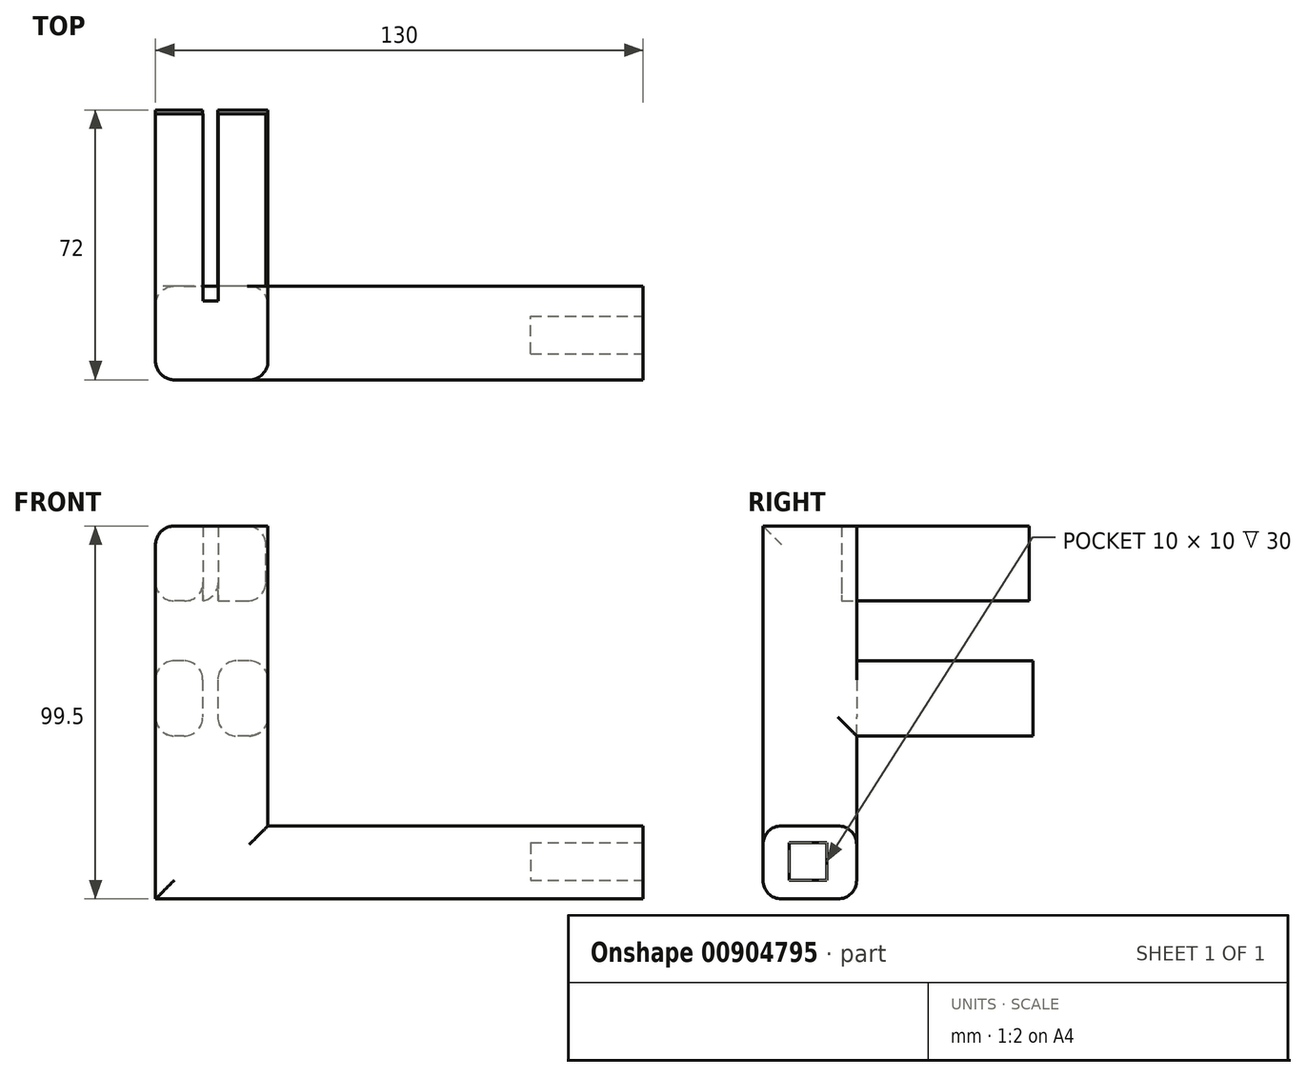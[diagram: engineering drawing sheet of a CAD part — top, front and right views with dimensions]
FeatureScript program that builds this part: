
annotation { "Feature Type Name" : "Feature", "Feature Type Description" : "" }
export const myFeature = defineFeature(function(context is Context, id is Id, definition is map)
    precondition{}
    {
        {
            var Q0;
            Q0=qCreatedBy(makeId("Front.planeOp"),FACE);
            var sketch = newSketch(context, id + "F0", { "sketchPlane" : qUnion([Q0])});
            skLineSegment(sketch, "E0", {"start": v(40.24, -41.34) * mm, "end": v(40.24, -41.2) * mm});
            skLineSegment(sketch, "E1", {"start": v(40.24, -41.34) * mm, "end": v(-89.76, -41.34) * mm});
            skLineSegment(sketch, "E2", {"start": v(-89.76, 58.16) * mm, "end": v(-59.76, 58.16) * mm});
            skLineSegment(sketch, "E3", {"start": v(-59.76, -21.84) * mm, "end": v(40.24, -21.84) * mm});
            skLineSegment(sketch, "E4", {"start": v(40.24, -21.84) * mm, "end": v(40.24, -41.2) * mm});
            skLineSegment(sketch, "E5", {"start": v(-59.76, 58.16) * mm, "end": v(-59.76, -21.84) * mm});
            skLineSegment(sketch, "E6", {"start": v(-89.76, 58.16) * mm, "end": v(-89.76, -41.34) * mm});
            skSolve(sketch);
        }
        {
            var Q0;
            Q0=makeQuery(id+"F0.imprint","IMPRINT",FACE,{"disambiguationData":[TD([[makeQuery(id+"F0.imprint","IMPRINT",EDGE,{"derivedFrom":sQuery(id+"F0.wireOp",EDGE,"E0")}),1.0]])]});
            extrude(context, id + "F1", {"entities" : qUnion([Q0]), "depth" : 25 * mm, "offsetDistance" : 25 * mm});
        }
        {
            var Q0;
            Q0=makeQuery(id+"F1.opExtrude","SWEPT_FACE",FACE,{"disambiguationData":[OSD([sQuery(id+"F0.wireOp",EDGE,"E2")])]});
            var sketch = newSketch(context, id + "F2", { "sketchPlane" : qUnion([Q0])});
            skLineSegment(sketch, "E7.bottom", {"start": v(-89.76, 46) * mm, "end": v(-60.31, 46) * mm});
            skLineSegment(sketch, "E7.top", {"start": v(-89.76, -9) * mm, "end": v(-60.31, -9) * mm});
            skLineSegment(sketch, "E7.left", {"start": v(-89.76, 46) * mm, "end": v(-89.76, -9) * mm});
            skLineSegment(sketch, "E7.right", {"start": v(-60.31, 46) * mm, "end": v(-60.31, -9) * mm});
            skSolve(sketch);
        }
        {
            var Q0;
            {var subQ0=sQuery(id+"F2.wireOp",EDGE,"E7.top");Q0=makeQuery(id+"F2.imprint","IMPRINT",FACE,{"disambiguationData":[TD([[makeQuery(id+"F2.imprint","IMPRINT",EDGE,{"derivedFrom":subQ0}),1.0]])]});}
            var Q1;
            {var subQ0=sQuery(id+"F2.wireOp",EDGE,"E7.bottom");Q1=makeQuery(id+"F2.imprint","IMPRINT",FACE,{"disambiguationData":[TD([[makeQuery(id+"F2.imprint","IMPRINT",EDGE,{"derivedFrom":subQ0}),-1.0]])]});}
            extrude(context, id + "F3", {"entities" : qUnion([Q0, Q1]), "operationType" : NewBodyOperationType.ADD, "oppositeDirection" : true, "depth" : 20 * mm, "offsetDistance" : 25 * mm});
        }
        {
            var Q0;
            Q0=makeQuery(id+"F3.opExtrude","SWEPT_FACE",FACE,{"disambiguationData":[OSD([sQuery(id+"F2.wireOp",EDGE,"E7.bottom")])]});
            var sketch = newSketch(context, id + "F4", { "sketchPlane" : qUnion([Q0])});
            skLineSegment(sketch, "E8.bottom", {"start": v(73.04, 58.16) * mm, "end": v(77.04, 58.16) * mm});
            skLineSegment(sketch, "E8.top", {"start": v(73.04, 38.16) * mm, "end": v(77.04, 38.16) * mm});
            skLineSegment(sketch, "E9", {"start": v(77.04, 58.16) * mm, "end": v(77.04, 38.16) * mm});
            skLineSegment(sketch, "E10", {"start": v(73.04, 58.16) * mm, "end": v(73.04, 38.16) * mm});
            skSolve(sketch);
        }
        {
            var Q0;
            Q0=makeQuery(id+"F4.imprint","IMPRINT",FACE,{"disambiguationData":[TD([[makeQuery(id+"F4.imprint","IMPRINT",EDGE,{"derivedFrom":sQuery(id+"F4.wireOp",EDGE,"E8.top")}),-1.0]])]});
            extrude(context, id + "F5", {"entities" : qUnion([Q0]), "operationType" : NewBodyOperationType.REMOVE, "oppositeDirection" : true, "depth" : 50 * mm, "offsetDistance" : 25 * mm});
        }
        {
            var Q0;
            Q0=makeQuery(id+"F1.opExtrude","CAP_FACE",FACE,{"disambiguationData":[OSD([sQuery(id+"F0.wireOp",EDGE,"E0"),sQuery(id+"F0.wireOp",EDGE,"E1"),sQuery(id+"F0.wireOp",EDGE,"0686c2bd-6ec9-4ceb-ab54-b0329b36704b"),sQuery(id+"F0.wireOp",EDGE,"E2"),sQuery(id+"F0.wireOp",EDGE,"96b1564c-ce13-4406-9d07-ae3dbd072935"),sQuery(id+"F0.wireOp",EDGE,"E3"),sQuery(id+"F0.wireOp",EDGE,"E4")])],"isStart":true});
            var sketch = newSketch(context, id + "F6", { "sketchPlane" : qUnion([Q0])});
            skLineSegment(sketch, "E11.bottom", {"start": v(59.76, 22.16) * mm, "end": v(89.76, 22.16) * mm});
            skLineSegment(sketch, "E11.top", {"start": v(59.76, 2.16) * mm, "end": v(89.76, 2.16) * mm});
            skLineSegment(sketch, "E11.left", {"start": v(59.76, 22.16) * mm, "end": v(59.76, 2.16) * mm});
            skLineSegment(sketch, "E11.right", {"start": v(89.76, 22.16) * mm, "end": v(89.76, 2.16) * mm});
            skLineSegment(sketch, "E12.bottom", {"start": v(73.16, 22.16) * mm, "end": v(77.16, 22.16) * mm});
            skLineSegment(sketch, "E12.top", {"start": v(73.16, 2.16) * mm, "end": v(77.16, 2.16) * mm});
            skLineSegment(sketch, "E12.left", {"start": v(73.16, 22.16) * mm, "end": v(73.16, 2.16) * mm});
            skLineSegment(sketch, "E12.right", {"start": v(77.16, 22.16) * mm, "end": v(77.16, 2.16) * mm});
            skSolve(sketch);
        }
        {
            var Q0;
            {var subQ0=sQuery(id+"F6.wireOp",EDGE,"E11.left");Q0=makeQuery(id+"F6.imprint","IMPRINT",FACE,{"disambiguationData":[TD([[makeQuery(id+"F6.imprint","IMPRINT",EDGE,{"derivedFrom":subQ0}),1.0]])]});}
            var Q1;
            {var subQ0=sQuery(id+"F6.wireOp",EDGE,"E11.right");Q1=makeQuery(id+"F6.imprint","IMPRINT",FACE,{"disambiguationData":[TD([[makeQuery(id+"F6.imprint","IMPRINT",EDGE,{"derivedFrom":subQ0}),-1.0]])]});}
            extrude(context, id + "F7", {"entities" : qUnion([Q0, Q1]), "operationType" : NewBodyOperationType.ADD, "depth" : 47 * mm, "offsetDistance" : 25 * mm, "hasSecondDirection" : true, "secondDirectionOppositeDirection" : true, "secondDirectionDepth" : 10 * mm});
        }
        {
            var Q0;
            Q0=makeQuery(id+"F1.opExtrude","SWEPT_FACE",FACE,{"disambiguationData":[OSD([sQuery(id+"F0.wireOp",EDGE,"E0"),sQuery(id+"F0.wireOp",EDGE,"E4")])]});
            var sketch = newSketch(context, id + "F8", { "sketchPlane" : qUnion([Q0])});
            skLineSegment(sketch, "E13.bottom", {"start": v(-18, -26.34) * mm, "end": v(-8, -26.34) * mm});
            skLineSegment(sketch, "E13.top", {"start": v(-18, -36.34) * mm, "end": v(-8, -36.34) * mm});
            skLineSegment(sketch, "E13.left", {"start": v(-18, -26.34) * mm, "end": v(-18, -36.34) * mm});
            skLineSegment(sketch, "E13.right", {"start": v(-8, -26.34) * mm, "end": v(-8, -36.34) * mm});
            skSolve(sketch);
        }
        {
            var Q0;
            Q0=makeQuery(id+"F8.imprint","IMPRINT",FACE,{"disambiguationData":[TD([[makeQuery(id+"F8.imprint","IMPRINT",EDGE,{"derivedFrom":sQuery(id+"F8.wireOp",EDGE,"E13.bottom")}),-1.0]])]});
            extrude(context, id + "F9", {"entities" : qUnion([Q0]), "operationType" : NewBodyOperationType.REMOVE, "oppositeDirection" : true, "depth" : 30 * mm, "offsetDistance" : 25 * mm});
        }
        {
            var Q0;
            Q0=makeQuery(id+"F3.opExtrude","CAP_EDGE",EDGE,{"disambiguationData":[OSD([sQuery(id+"F2.wireOp",EDGE,"E7.right")])],"isStart":true});
            var Q1;
            Q1=makeQuery(id+"F5.boolean.opBoolean","COPY",EDGE,{"derivedFrom":makeQuery(id+"F5.opExtrude","SWEPT_EDGE",EDGE,{"disambiguationData":[OSD([sQuery(id+"F2.wireOp",EDGE,"E7.bottom"),sQuery(id+"F4.wireOp",EDGE,"E10"),sQuery(id+"F4.wireOp",EDGE,"E8.bottom")])]})});
            var Q2;
            Q2=makeQuery(id+"F3.opExtrude","CAP_EDGE",EDGE,{"disambiguationData":[OSD([sQuery(id+"F2.wireOp",EDGE,"E7.right")])],"isStart":false});
            var Q3;
            {var subQ0=sQuery(id+"F2.wireOp",EDGE,"E7.bottom");var subQ1=sQuery(id+"F4.wireOp",EDGE,"E10");Q3=makeQuery(id+"F5.boolean.opBoolean","COPY",EDGE,{"disambiguationData":[topologyDisambiguationEdgeConnected([makeQuery(id+"F3.opExtrude","CAP_FACE",FACE,{"disambiguationData":[OSD([subQ0,sQuery(id+"F2.wireOp",EDGE,"E7.top"),sQuery(id+"F2.wireOp",EDGE,"E7.left"),sQuery(id+"F2.wireOp",EDGE,"E7.right")])],"isStart":false})])],"derivedFrom":makeQuery(id+"F5.opExtrude","SWEPT_EDGE",EDGE,{"disambiguationData":[OSD([subQ0,sQuery(id+"F4.wireOp",EDGE,"E8.top"),subQ1])]})});}
            var Q4;
            {var subQ0=sQuery(id+"F2.wireOp",EDGE,"E7.bottom");var subQ1=sQuery(id+"F4.wireOp",EDGE,"E9");Q4=makeQuery(id+"F5.boolean.opBoolean","COPY",EDGE,{"disambiguationData":[topologyDisambiguationEdgeConnected([makeQuery(id+"F3.opExtrude","CAP_FACE",FACE,{"disambiguationData":[OSD([subQ0,sQuery(id+"F2.wireOp",EDGE,"E7.top"),sQuery(id+"F2.wireOp",EDGE,"E7.left"),sQuery(id+"F2.wireOp",EDGE,"E7.right")])],"isStart":false})])],"derivedFrom":makeQuery(id+"F5.opExtrude","SWEPT_EDGE",EDGE,{"disambiguationData":[OSD([subQ0,sQuery(id+"F4.wireOp",EDGE,"E8.top"),subQ1])]})});}
            var Q5;
            Q5=makeQuery(id+"F3.opExtrude","CAP_EDGE",EDGE,{"disambiguationData":[OSD([sQuery(id+"F2.wireOp",EDGE,"E7.left")])],"isStart":false});
            var Q6;
            Q6=makeQuery(id+"F3.boolean.opBoolean","MERGE",EDGE,{"derivedFrom":[makeQuery(id+"F1.opExtrude","SWEPT_EDGE",EDGE,{"disambiguationData":[OSD([sQuery(id+"F0.wireOp",EDGE,"E2"),sQuery(id+"F0.wireOp",EDGE,"E6")])]}),makeQuery(id+"F3.opExtrude","CAP_EDGE",EDGE,{"disambiguationData":[OSD([sQuery(id+"F2.wireOp",EDGE,"E7.left")])],"isStart":true})]});
            var Q7;
            Q7=makeQuery(id+"F5.boolean.opBoolean","COPY",EDGE,{"derivedFrom":makeQuery(id+"F5.opExtrude","SWEPT_EDGE",EDGE,{"disambiguationData":[OSD([sQuery(id+"F2.wireOp",EDGE,"E7.bottom"),sQuery(id+"F4.wireOp",EDGE,"E9"),sQuery(id+"F4.wireOp",EDGE,"E8.bottom")])]})});
            var Q8;
            Q8=makeQuery(id+"F7.opExtrude","SWEPT_EDGE",EDGE,{"disambiguationData":[OSD([sQuery(id+"F0.wireOp",EDGE,"E6"),sQuery(id+"F6.wireOp",EDGE,"E11.top"),sQuery(id+"F6.wireOp",EDGE,"E11.right")])]});
            var Q9;
            Q9=makeQuery(id+"F7.opExtrude","SWEPT_EDGE",EDGE,{"disambiguationData":[OSD([sQuery(id+"F0.wireOp",EDGE,"E6"),sQuery(id+"F6.wireOp",EDGE,"E11.bottom"),sQuery(id+"F6.wireOp",EDGE,"E11.right")])]});
            var Q10;
            Q10=makeQuery(id+"F7.opExtrude","SWEPT_EDGE",EDGE,{"disambiguationData":[OSD([sQuery(id+"F6.wireOp",EDGE,"E11.bottom"),sQuery(id+"F6.wireOp",EDGE,"E12.bottom"),sQuery(id+"F6.wireOp",EDGE,"E12.right")])]});
            var Q11;
            Q11=makeQuery(id+"F7.opExtrude","SWEPT_EDGE",EDGE,{"disambiguationData":[OSD([sQuery(id+"F6.wireOp",EDGE,"E11.top"),sQuery(id+"F6.wireOp",EDGE,"E12.top"),sQuery(id+"F6.wireOp",EDGE,"E12.right")])]});
            var Q12;
            Q12=makeQuery(id+"F7.opExtrude","SWEPT_EDGE",EDGE,{"disambiguationData":[OSD([sQuery(id+"F6.wireOp",EDGE,"E11.top"),sQuery(id+"F6.wireOp",EDGE,"E12.top"),sQuery(id+"F6.wireOp",EDGE,"E12.left")])]});
            var Q13;
            Q13=makeQuery(id+"F7.opExtrude","SWEPT_EDGE",EDGE,{"disambiguationData":[OSD([sQuery(id+"F0.wireOp",EDGE,"E5"),sQuery(id+"F6.wireOp",EDGE,"E11.top"),sQuery(id+"F6.wireOp",EDGE,"E11.left")])]});
            var Q14;
            Q14=makeQuery(id+"F7.opExtrude","SWEPT_EDGE",EDGE,{"disambiguationData":[OSD([sQuery(id+"F0.wireOp",EDGE,"E5"),sQuery(id+"F6.wireOp",EDGE,"E11.bottom"),sQuery(id+"F6.wireOp",EDGE,"E11.left")])]});
            var Q15;
            Q15=makeQuery(id+"F7.opExtrude","SWEPT_EDGE",EDGE,{"disambiguationData":[OSD([sQuery(id+"F6.wireOp",EDGE,"E11.bottom"),sQuery(id+"F6.wireOp",EDGE,"E12.bottom"),sQuery(id+"F6.wireOp",EDGE,"E12.left")])]});
            var Q16;
            Q16=makeQuery(id+"F1.opExtrude","CAP_EDGE",EDGE,{"disambiguationData":[OSD([sQuery(id+"F0.wireOp",EDGE,"E3")])],"isStart":true});
            var Q17;
            Q17=makeQuery(id+"F1.opExtrude","CAP_EDGE",EDGE,{"disambiguationData":[OSD([sQuery(id+"F0.wireOp",EDGE,"E1")])],"isStart":true});
            var Q18;
            {var subQ0=sQuery(id+"F0.wireOp",EDGE,"E6");var subQ1=sQuery(id+"F0.wireOp",EDGE,"E1");var subQ4=makeQuery(id+"F1.opExtrude","CAP_EDGE",EDGE,{"disambiguationData":[OSD([subQ0])],"isStart":true});Q18=makeQuery(id+"F7.boolean.opBoolean","SPLIT",EDGE,{"disambiguationData":[TD([makeQuery(id+"F1.opExtrude","SWEPT_FACE",FACE,{"disambiguationData":[OSD([subQ1])]})])],"derivedFrom":subQ4});}
            var Q19;
            {var subQ2=sQuery(id+"F0.wireOp",EDGE,"E5");var subQ3=makeQuery(id+"F1.opExtrude","CAP_EDGE",EDGE,{"disambiguationData":[OSD([subQ2])],"isStart":true});var subQ4=sQuery(id+"F0.wireOp",EDGE,"E3");Q19=makeQuery(id+"F7.boolean.opBoolean","SPLIT",EDGE,{"disambiguationData":[TD([makeQuery(id+"F1.opExtrude","SWEPT_FACE",FACE,{"disambiguationData":[OSD([subQ4])]})])],"derivedFrom":subQ3});}
            var Q20;
            Q20=makeQuery(id+"F1.opExtrude","CAP_EDGE",EDGE,{"disambiguationData":[OSD([sQuery(id+"F0.wireOp",EDGE,"E6")])],"isStart":false});
            var Q21;
            Q21=makeQuery(id+"F1.opExtrude","CAP_EDGE",EDGE,{"disambiguationData":[OSD([sQuery(id+"F0.wireOp",EDGE,"E1")])],"isStart":false});
            var Q22;
            Q22=makeQuery(id+"F1.opExtrude","CAP_EDGE",EDGE,{"disambiguationData":[OSD([sQuery(id+"F0.wireOp",EDGE,"E3")])],"isStart":false});
            var Q23;
            Q23=makeQuery(id+"F1.opExtrude","CAP_EDGE",EDGE,{"disambiguationData":[OSD([sQuery(id+"F0.wireOp",EDGE,"E5")])],"isStart":false});
            fillet(context, id + "F10", {"entities" : qUnion([Q0, Q1, Q2, Q3, Q4, Q5, Q6, Q7, Q8, Q9, Q10, Q11, Q12, Q13, Q14, Q15, Q16, Q17, Q18, Q19, Q20, Q21, Q22, Q23]), "radius" : 5 * mm, "tangentPropagation" : true, "allowEdgeOverflow" : false});
        }
    });
